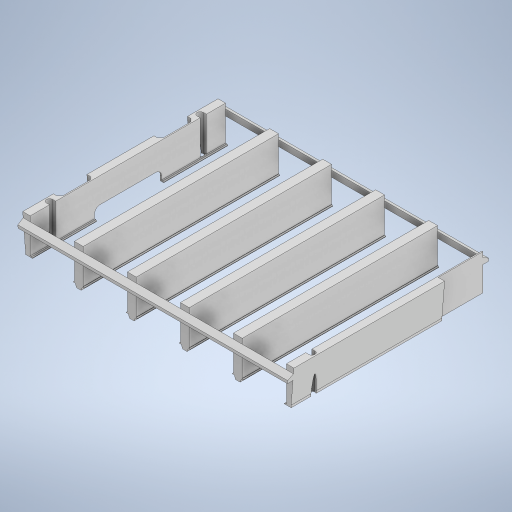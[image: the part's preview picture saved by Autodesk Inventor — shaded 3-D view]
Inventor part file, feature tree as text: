
AUTODESK INVENTOR PART (.ipt)
format: ipt  version: 2023 (Build 270158000, 158)  size: 726,016 bytes
history: native  units: mm
features: projected_geometry x17, sketch x13, extrude x12, plane x7, chamfer x3, draft x2, fillet x1, pattern_linear x1, hole x1
ambient origin geometry x8: Origin, YZ Plane, XZ Plane, XY Plane, X Axis, Y Axis, Z Axis, Center Point
bodies: Solid1 (feature_tree)
feature tree (57):
  extrude  "Extrusion1"  Depth=70.0mm
  extrude  "Extrusion2"  Depth=19.0mm
  extrude  "Extrusion3"  Depth=3.2mm
  plane  "Work Plane1"
  extrude  "Extrusion4"  Depth=12.0mm TaperAngle=0.0deg
  draft  "FaceDraft1"
  draft  "FaceDraft2"
  extrude  "Extrusion5"  Depth=1.6mm
  extrude  "Extrusion6"  Depth=12.0mm TaperAngle=0.0deg
  extrude  "Extrusion7"  TaperAngle=0.0deg  [1 undecoded]
  extrude  "Extrusion8"  Depth=2.0mm
  fillet  "Fillet1"  Radius=1.0mm
  chamfer  "Chamfer1"  [1 undecoded]
  plane  "Work Plane2"
  pattern_linear  "Rectangular Pattern1"  Spacing1=0.0mm  [1 undecoded]
  plane  "Work Plane7"
  hole  "Hole2"  [1 undecoded]
  extrude  "Extrusion11"  Depth=11.0mm
  extrude  "Extrusion12"  Depth=0.4mm
  extrude  "Extrusion13"  TaperAngle=0.0deg  [1 undecoded]
  extrude  "Extrusion14"  Depth=25.0mm
  chamfer  "Chamfer2"  Distance=3.0mm
  chamfer  "Chamfer3"  Distance=2.0mm
  sketch  "Sketch1"  dims[d0=97.2mm d1=70.0mm]
  sketch  "Sketch2"  dims[d2=2.7mm d3=40.0mm d5=19.0mm d6=10.0mm d8=10.0mm]
  projected_geometry  "Projected Loop1"
  sketch  "Sketch3"  dims[d10=19.0mm d11=3.2mm]
  sketch  "Sketch4"  dims[d12=19.0mm d13=12.0mm d14=0.0mm]
  sketch  "Sketch5"  dims[d17=2.0mm d18=1.6mm]
  projected_geometry  "Projected Loop2"
  projected_geometry  "Projected Loop3"
  sketch  "Sketch6"  dims[d19=40.0mm d21=19.0mm d22=10.0mm d24=10.0mm d26=12.0mm d27=0.0mm]
  sketch  "Sketch7"  dims[d28=1.0mm d29=0.0mm d30=0.0mm]
  sketch  "Sketch8"  dims[d31=-3.0mm d32=2.0mm d33=1.0mm d34=0.0mm]
  plane  "Work Plane3"
  plane  "Work Plane4"
  plane  "Work Plane5"
  plane  "Work Plane6"
  projected_geometry  "Projected Loop4"
  projected_geometry  "Projected Loop5"
  projected_geometry  "Projected Loop6"
  projected_geometry  "Projected Loop7"
  sketch  "Sketch13"  dims[d35=30.0deg]
  sketch  "Sketch14"  dims[d36=2.0mm]
  sketch  "Sketch15"  dims[d37=30.0deg d38=0.0mm d39=0.0mm]
  projected_geometry  "Projected Loop11"
  projected_geometry  "Projected Loop12"
  projected_geometry  "Projected Loop13"
  projected_geometry  "Projected Loop14"
  projected_geometry  "Projected Loop15"
  projected_geometry  "Projected Loop16"
  sketch  "Sketch16"  dims[d40=0.4mm]
  sketch  "Sketch17"  dims[d41=18.0mm d42=0.0mm d43=0.0mm d45=11.0mm d47=11.0mm d50=0.4mm d51=0.0mm d52=0.0mm d53=25.0mm d54=3.0mm d55=0.0mm d56=2.0mm d57=1.0mm d58=2.0mm d59=45.0deg d60=50.0mm d62=19.0mm d63=12.0mm d64=12.0mm d84=2.2mm d85=6.0mm d86=4.0mm d87=2.0mm d88=90.0deg d89=8.0mm d90=0.0mm d91=94.0mm d92=54.0mm d94=10.0mm d95=0.0mm d96=0.8mm d97=0.0mm d98=4.0mm d99=0.8mm d100=0.4mm d101=0.0mm d102=0.0mm d103=0.0mm d104=0.3mm d105=2.0mm d106=45.0deg d107=0.3mm d108=2.0mm d109=45.0deg]
  projected_geometry  "Projected Loop17"
  projected_geometry  "Projected Loop18"
  projected_geometry  "Projected Loop19"
  projected_geometry  "Projected Loop20"
note: 5 required parameter values undecoded (feature->parameter linkage not recoverable at this tier; creation-order binding heuristic only, values carry confidence <= 0.55)
